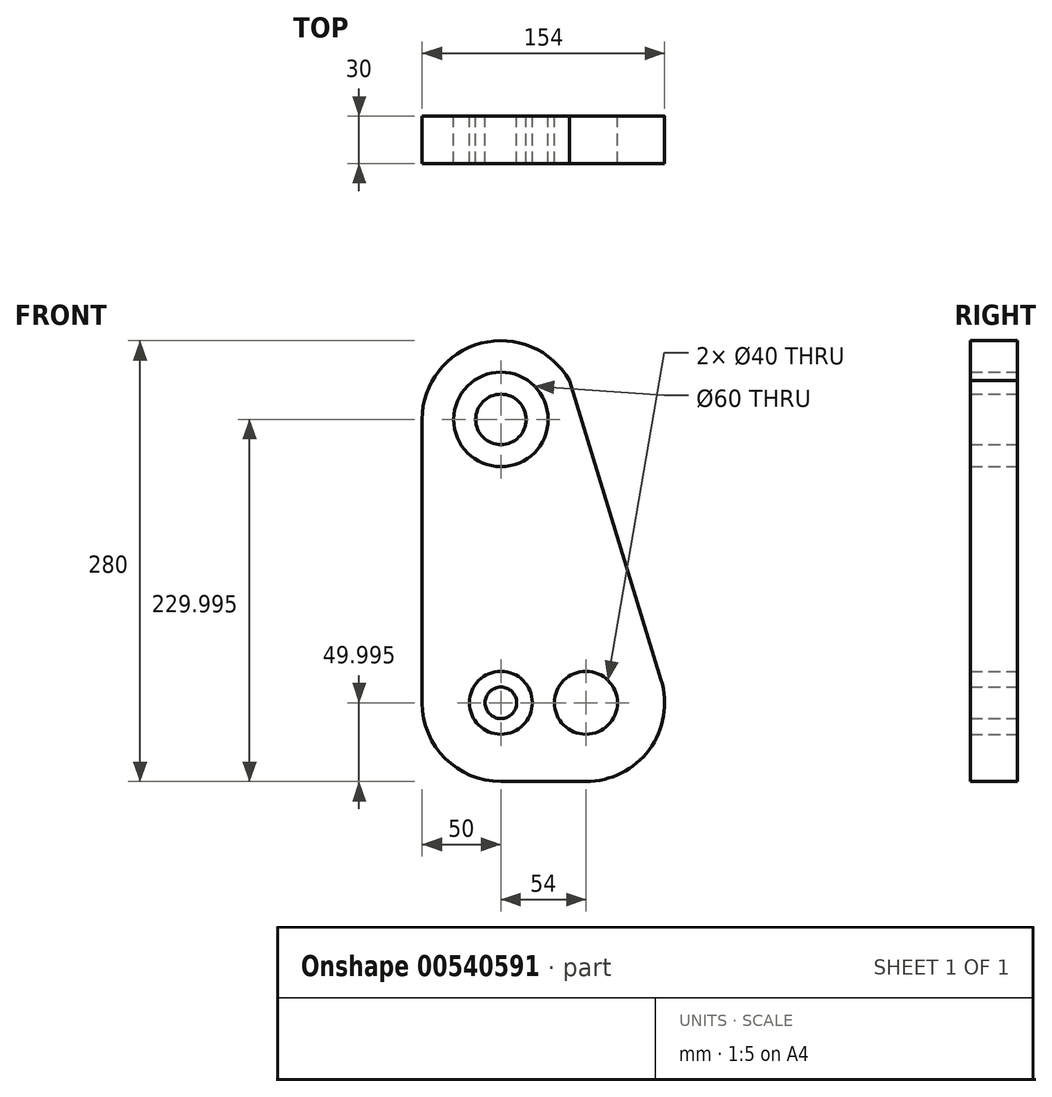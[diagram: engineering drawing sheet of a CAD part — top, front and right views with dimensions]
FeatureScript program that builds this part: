
annotation { "Feature Type Name" : "Feature", "Feature Type Description" : "" }
export const myFeature = defineFeature(function(context is Context, id is Id, definition is map)
    precondition{}
    {
        {
            var Q0;
            Q0=qCreatedBy(makeId("Front.planeOp"),FACE);
            var sketch = newSketch(context, id + "F0", { "sketchPlane" : qUnion([Q0])});
            skArc(sketch, "E0", {"start": v(-50, -66.88) * mm, "mid": v(-35.36, -102.24) * mm, "end": v(0, -116.88) * mm});
            skArc(sketch, "E1", {"start": v(43.54, 137.7) * mm, "mid": v(-12.7, 161.47) * mm, "end": v(-50, 113.12) * mm});
            skArc(sketch, "E2", {"start": v(54, -116.88) * mm, "mid": v(94.2, -96.6) * mm, "end": v(101.8, -52.22) * mm});
            skLineSegment(sketch, "E3", {"start": v(-50, 113.12) * mm, "end": v(-50, -66.88) * mm});
            skLineSegment(sketch, "E4", {"start": v(0, -116.88) * mm, "end": v(54, -116.88) * mm});
            skPoint(sketch, "E5.orphan", {"position": v(50, 113.12) * mm});
            skCircle(sketch, "E6", {"center": v(0, -66.88) * mm, "radius": 20 * mm});
            skCircle(sketch, "E7", {"center": v(54, -66.88) * mm, "radius": 20 * mm});
            skCircle(sketch, "E8", {"center": v(0, -66.88) * mm, "radius": 10 * mm});
            skCircle(sketch, "E9", {"center": v(0, 113.12) * mm, "radius": 30 * mm});
            skCircle(sketch, "E10", {"center": v(0, 113.12) * mm, "radius": 16 * mm});
            skLineSegment(sketch, "E11", {"start": v(43.54, 137.7) * mm, "end": v(101.8, -52.22) * mm});
            skSolve(sketch);
        }
        {
            var Q0;
            Q0=makeQuery(id+"F0.imprint","IMPRINT",FACE,{"disambiguationData":[TD([[makeQuery(id+"F0.imprint","IMPRINT",EDGE,{"derivedFrom":sQuery(id+"F0.wireOp",EDGE,"E0")}),1.0]])]});
            var Q1;
            Q1=makeQuery(id+"F0.imprint","IMPRINT",FACE,{"disambiguationData":[TD([[makeQuery(id+"F0.imprint","IMPRINT",EDGE,{"derivedFrom":sQuery(id+"F0.wireOp",EDGE,"E8")}),1.0]])]});
            var Q2;
            Q2=makeQuery(id+"F0.imprint","IMPRINT",FACE,{"disambiguationData":[TD([[makeQuery(id+"F0.imprint","IMPRINT",EDGE,{"derivedFrom":sQuery(id+"F0.wireOp",EDGE,"E10")}),1.0]])]});
            extrude(context, id + "F1", {"entities" : qUnion([Q0, Q1, Q2]), "depth" : 30 * mm, "offsetDistance" : 25 * mm});
        }
    });
